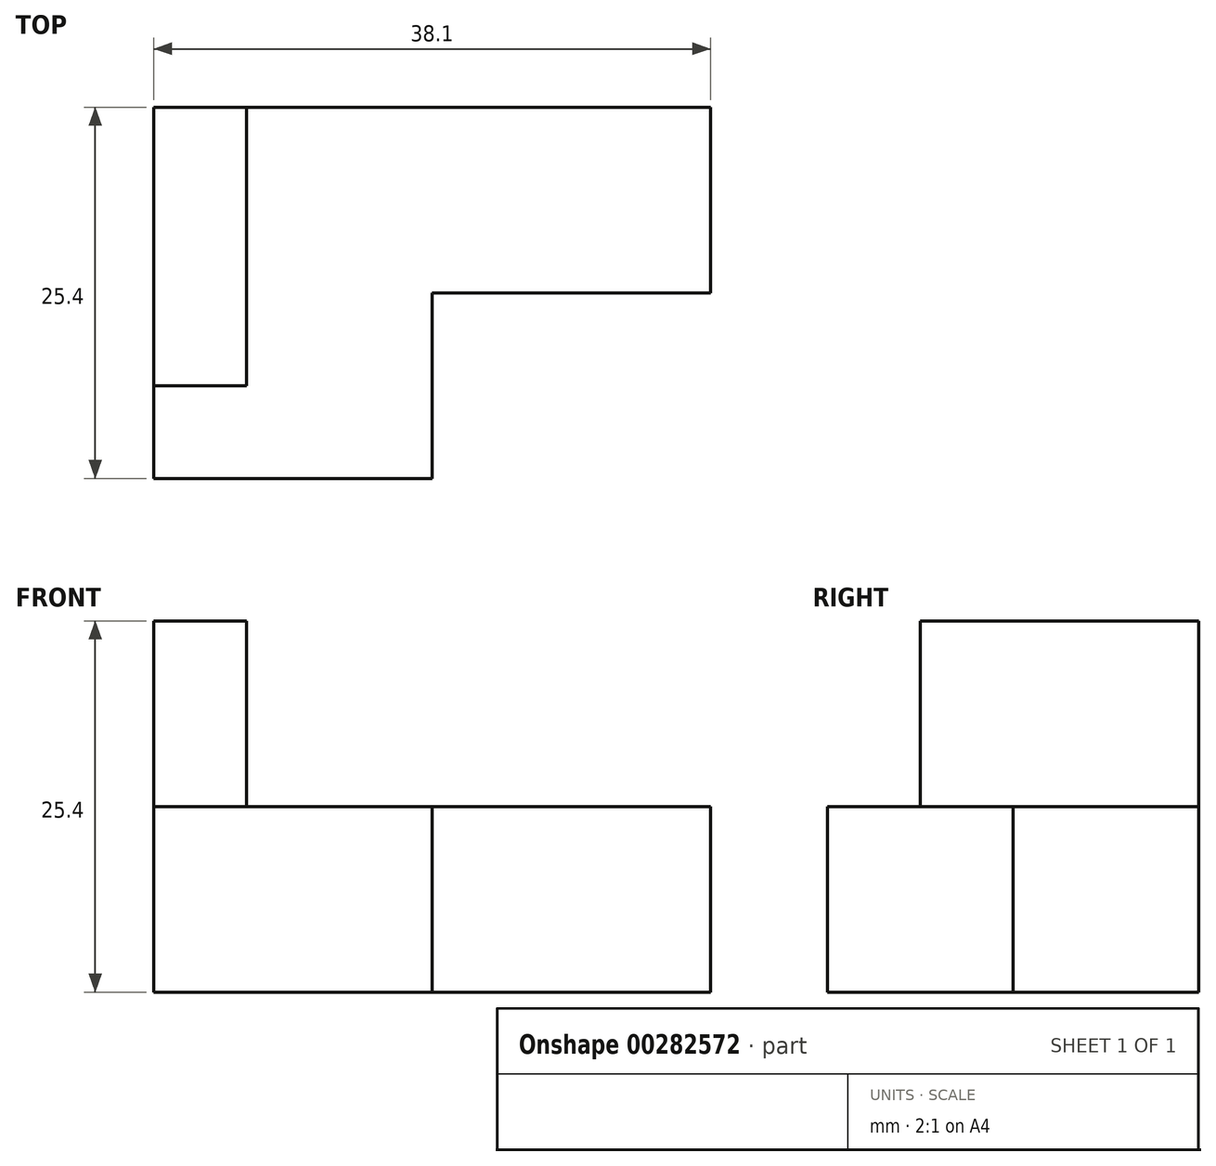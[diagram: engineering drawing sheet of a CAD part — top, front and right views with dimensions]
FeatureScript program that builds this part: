
annotation { "Feature Type Name" : "Feature", "Feature Type Description" : "" }
export const myFeature = defineFeature(function(context is Context, id is Id, definition is map)
    precondition{}
    {
        {
            var Q0;
            Q0=qCreatedBy(makeId("Front.planeOp"),FACE);
            var sketch = newSketch(context, id + "F0", { "sketchPlane" : qUnion([Q0])});
            skLineSegment(sketch, "E0", {"start": v(0, 0) * mm, "end": v(0, 25.4) * mm});
            skLineSegment(sketch, "E1", {"start": v(0, 25.4) * mm, "end": v(6.35, 25.4) * mm});
            skLineSegment(sketch, "E2", {"start": v(6.35, 25.4) * mm, "end": v(6.35, 12.7) * mm});
            skLineSegment(sketch, "E3", {"start": v(6.35, 12.7) * mm, "end": v(38.1, 12.7) * mm});
            skLineSegment(sketch, "E4", {"start": v(38.1, 12.7) * mm, "end": v(38.1, 0) * mm});
            skLineSegment(sketch, "E5", {"start": v(38.1, 0) * mm, "end": v(0, 0) * mm});
            skLineSegment(sketch, "E6", {"start": v(19.05, 0) * mm, "end": v(19.05, 12.7) * mm});
            skLineSegment(sketch, "E7", {"start": v(6.35, 12.7) * mm, "end": v(0, 12.7) * mm});
            skSolve(sketch);
        }
        {
            var Q0;
            {var subQ0=sQuery(id+"F0.wireOp",EDGE,"E1");Q0=makeQuery(id+"F0.imprint","IMPRINT",FACE,{"disambiguationData":[TD([[makeQuery(id+"F0.imprint","IMPRINT",EDGE,{"derivedFrom":subQ0}),-1.0]])]});}
            var Q1;
            {var subQ3=sQuery(id+"F0.wireOp",EDGE,"E6");Q1=makeQuery(id+"F0.imprint","IMPRINT",FACE,{"disambiguationData":[TD([[makeQuery(id+"F0.imprint","IMPRINT",EDGE,{"derivedFrom":subQ3}),1.0]])]});}
            var Q2;
            {var subQ0=sQuery(id+"F0.wireOp",EDGE,"E4");Q2=makeQuery(id+"F0.imprint","IMPRINT",FACE,{"disambiguationData":[TD([[makeQuery(id+"F0.imprint","IMPRINT",EDGE,{"derivedFrom":subQ0}),-1.0]])]});}
            extrude(context, id + "F1", {"entities" : qUnion([Q0, Q1, Q2]), "oppositeDirection" : true, "depth" : 25.4 * mm});
        }
        {
            var Q0;
            {var subQ0=sQuery(id+"F0.wireOp",EDGE,"E4");Q0=makeQuery(id+"F0.imprint","IMPRINT",FACE,{"disambiguationData":[TD([[makeQuery(id+"F0.imprint","IMPRINT",EDGE,{"derivedFrom":subQ0}),-1.0]])]});}
            extrude(context, id + "F2", {"entities" : qUnion([Q0]), "operationType" : NewBodyOperationType.REMOVE, "oppositeDirection" : true, "depth" : 12.7 * mm});
        }
        {
            var Q0;
            {var subQ0=sQuery(id+"F0.wireOp",EDGE,"E1");Q0=makeQuery(id+"F0.imprint","IMPRINT",FACE,{"disambiguationData":[TD([[makeQuery(id+"F0.imprint","IMPRINT",EDGE,{"derivedFrom":subQ0}),-1.0]])]});}
            extrude(context, id + "F3", {"entities" : qUnion([Q0]), "operationType" : NewBodyOperationType.REMOVE, "oppositeDirection" : true, "depth" : 6.35 * mm});
        }
    });
